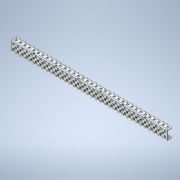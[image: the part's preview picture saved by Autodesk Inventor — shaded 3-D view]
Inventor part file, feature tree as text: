
AUTODESK INVENTOR PART (.ipt)
format: ipt  version: 2020 (Build 240168000, 168)  size: 1,510,912 bytes
history: native  units: in
note: dims shown in document units (in); Inventor stores cm internally (conversion verified against a paired STEP export)
features: other x210, plane x8, pattern_linear x5, sheet_metal_op x1
ambient origin geometry x8: Origin, YZ Plane, XZ Plane, XY Plane, X Axis, Y Axis, Z Axis, Center Point
bodies: Solid1 (feature_tree)
feature tree (224):
  other  "Work Axis1"
  pattern_linear  "Rectangular Pattern1"  Count1=35 Spacing1=0.5in
  other  "Work Axis71"
  pattern_linear  "Rectangular Pattern2"  Count1=34 Spacing1=0.5in
  other  "Work Axis105"
  pattern_linear  "Rectangular Pattern3"  Count1=35 Spacing1=0.5in
  plane  "Work Plane8"
  plane  "Work Plane7"
  other  "Work Axis140"
  pattern_linear  "Rectangular Pattern4"  Count1=35 Spacing1=0.5in
  other  "Work Axis282"
  pattern_linear  "Rectangular Pattern8"  Count1=35 Spacing1=0.5in
  plane  "Work Plane1"
  plane  "Work Plane2"
  other  "Work Axis2"
  other  "Work Axis3"
  other  "Work Axis4"
  other  "Work Axis5"
  other  "Work Axis6"
  other  "Work Axis7"
  other  "Work Axis8"
  other  "Work Axis9"
  other  "Work Axis10"
  other  "Work Axis11"
  other  "Work Axis12"
  other  "Work Axis13"
  other  "Work Axis14"
  other  "Work Axis15"
  other  "Work Axis16"
  other  "Work Axis17"
  other  "Work Axis18"
  other  "Work Axis19"
  other  "Work Axis20"
  other  "Work Axis21"
  other  "Work Axis22"
  other  "Work Axis23"
  other  "Work Axis24"
  other  "Work Axis25"
  other  "Work Axis26"
  other  "Work Axis27"
  other  "Work Axis28"
  other  "Work Axis29"
  other  "Work Axis30"
  other  "Work Axis31"
  other  "Work Axis32"
  other  "Work Axis33"
  other  "Work Axis34"
  other  "Work Axis35"
  other  "Work Axis36"
  other  "Work Axis37"
  other  "Work Axis38"
  other  "Work Axis39"
  other  "Work Axis40"
  other  "Work Axis41"
  other  "Work Axis42"
  other  "Work Axis43"
  other  "Work Axis44"
  other  "Work Axis45"
  other  "Work Axis46"
  other  "Work Axis47"
  other  "Work Axis48"
  other  "Work Axis49"
  other  "Work Axis50"
  other  "Work Axis51"
  other  "Work Axis52"
  other  "Work Axis53"
  other  "Work Axis54"
  other  "Work Axis55"
  other  "Work Axis56"
  other  "Work Axis57"
  other  "Work Axis58"
  other  "Work Axis59"
  other  "Work Axis60"
  other  "Work Axis61"
  other  "Work Axis62"
  other  "Work Axis63"
  other  "Work Axis64"
  other  "Work Axis65"
  other  "Work Axis66"
  other  "Work Axis67"
  other  "Work Axis68"
  other  "Work Axis69"
  other  "Work Axis70"
  plane  "Work Plane3"
  plane  "Work Plane4"
  other  "Work Axis72"
  other  "Work Axis73"
  other  "Work Axis74"
  other  "Work Axis75"
  other  "Work Axis76"
  other  "Work Axis77"
  other  "Work Axis78"
  other  "Work Axis79"
  other  "Work Axis80"
  other  "Work Axis81"
  other  "Work Axis82"
  other  "Work Axis83"
  other  "Work Axis84"
  other  "Work Axis85"
  other  "Work Axis86"
  other  "Work Axis87"
  other  "Work Axis88"
  other  "Work Axis89"
  other  "Work Axis90"
  other  "Work Axis91"
  other  "Work Axis92"
  other  "Work Axis93"
  other  "Work Axis94"
  other  "Work Axis95"
  other  "Work Axis96"
  other  "Work Axis97"
  other  "Work Axis98"
  other  "Work Axis99"
  other  "Work Axis100"
  other  "Work Axis101"
  other  "Work Axis102"
  other  "Work Axis103"
  other  "Work Axis104"
  plane  "Work Plane5"
  plane  "Work Plane6"
  other  "Work Axis106"
  other  "Work Axis107"
  other  "Work Axis108"
  other  "Work Axis109"
  other  "Work Axis110"
  other  "Work Axis111"
  other  "Work Axis112"
  other  "Work Axis113"
  other  "Work Axis114"
  other  "Work Axis115"
  other  "Work Axis116"
  other  "Work Axis117"
  other  "Work Axis118"
  other  "Work Axis119"
  other  "Work Axis120"
  other  "Work Axis121"
  other  "Work Axis122"
  other  "Work Axis123"
  other  "Work Axis124"
  other  "Work Axis125"
  other  "Work Axis126"
  other  "Work Axis127"
  other  "Work Axis128"
  other  "Work Axis129"
  other  "Work Axis130"
  other  "Work Axis131"
  other  "Work Axis132"
  other  "Work Axis133"
  other  "Work Axis134"
  other  "Work Axis135"
  other  "Work Axis136"
  other  "Work Axis137"
  other  "Work Axis138"
  other  "Work Axis139"
  other  "Work Axis141"
  other  "Work Axis142"
  other  "Work Axis143"
  other  "Work Axis144"
  other  "Work Axis145"
  other  "Work Axis146"
  other  "Work Axis147"
  other  "Work Axis148"
  other  "Work Axis149"
  other  "Work Axis150"
  other  "Work Axis151"
  other  "Work Axis152"
  other  "Work Axis153"
  other  "Work Axis154"
  other  "Work Axis155"
  other  "Work Axis156"
  other  "Work Axis157"
  other  "Work Axis158"
  other  "Work Axis159"
  other  "Work Axis160"
  other  "Work Axis161"
  other  "Work Axis162"
  other  "Work Axis163"
  other  "Work Axis164"
  other  "Work Axis165"
  other  "Work Axis166"
  other  "Work Axis167"
  other  "Work Axis168"
  other  "Work Axis169"
  other  "Work Axis170"
  other  "Work Axis171"
  other  "Work Axis172"
  other  "Work Axis173"
  other  "Work Axis174"
  other  "Work Point2"
  other  "Work Axis283"
  other  "Work Axis284"
  other  "Work Axis285"
  other  "Work Axis286"
  other  "Work Axis287"
  other  "Work Axis288"
  other  "Work Axis289"
  other  "Work Axis290"
  other  "Work Axis291"
  other  "Work Axis292"
  other  "Work Axis293"
  other  "Work Axis294"
  other  "Work Axis295"
  other  "Work Axis296"
  other  "Work Axis297"
  other  "Work Axis298"
  other  "Work Axis299"
  other  "Work Axis300"
  other  "Work Axis301"
  other  "Work Axis302"
  other  "Work Axis303"
  other  "Work Axis304"
  other  "Work Axis305"
  other  "Work Axis306"
  other  "Work Axis307"
  other  "Work Axis308"
  other  "Work Axis309"
  other  "Work Axis310"
  other  "Work Axis311"
  other  "Work Axis312"
  other  "Work Axis313"
  other  "Work Axis314"
  other  "Work Axis315"
  other  "Work Axis316"
  sheet_metal_op  "Fold1"
